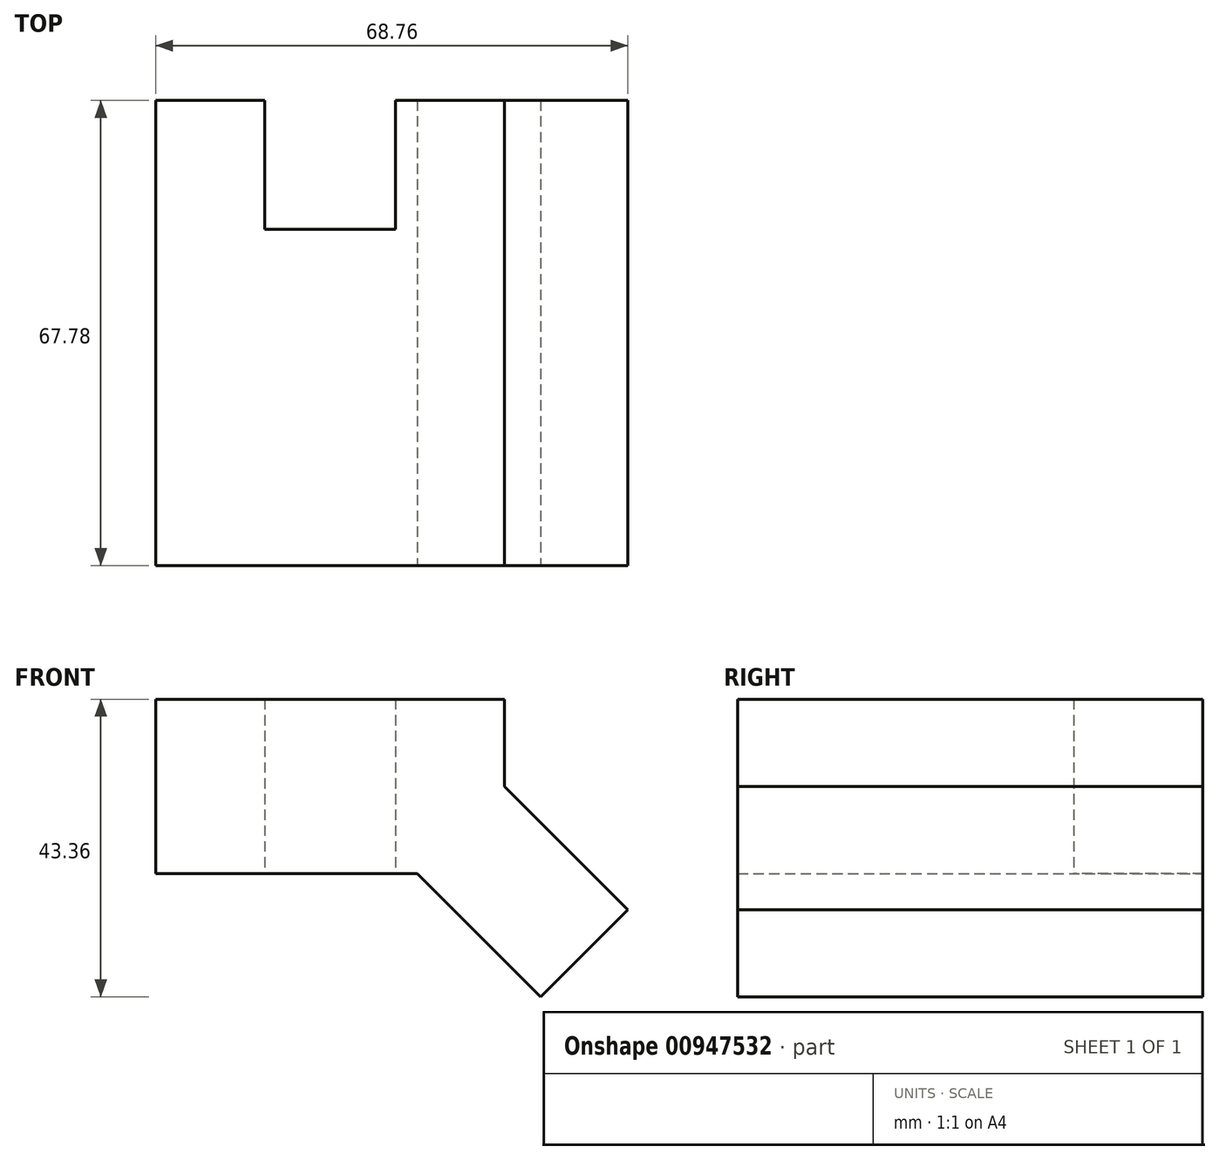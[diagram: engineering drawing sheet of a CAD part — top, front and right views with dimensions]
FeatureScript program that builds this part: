
annotation { "Feature Type Name" : "Feature", "Feature Type Description" : "" }
export const myFeature = defineFeature(function(context is Context, id is Id, definition is map)
    precondition{}
    {
        {
            var Q0;
            Q0=qCreatedBy(makeId("Top.planeOp"),FACE);
            var sketch = newSketch(context, id + "F0", { "sketchPlane" : qUnion([Q0])});
            skLineSegment(sketch, "E0.bottom", {"start": v(25.4, -33.9) * mm, "end": v(-25.4, -33.9) * mm});
            skLineSegment(sketch, "E0.top", {"start": v(25.4, 33.9) * mm, "end": v(-25.4, 33.9) * mm});
            skLineSegment(sketch, "E0.left", {"start": v(25.4, -33.9) * mm, "end": v(25.4, 33.9) * mm});
            skLineSegment(sketch, "E0.right", {"start": v(-25.4, -33.9) * mm, "end": v(-25.4, 33.9) * mm});
            skPoint(sketch, "E0.middle", {"position": v(0, 0) * mm});
            skLineSegment(sketch, "E1.bottom", {"start": v(-9.52, 33.9) * mm, "end": v(9.52, 33.9) * mm});
            skLineSegment(sketch, "E1.top", {"start": v(-9.52, 15.1) * mm, "end": v(9.53, 15.1) * mm});
            skLineSegment(sketch, "E1.left", {"start": v(-9.52, 33.9) * mm, "end": v(-9.52, 15.1) * mm});
            skLineSegment(sketch, "E1.right", {"start": v(9.53, 33.9) * mm, "end": v(9.53, 15.1) * mm});
            skPoint(sketch, "E2", {"position": v(-9.52, 33.9) * mm});
            skPoint(sketch, "E3", {"position": v(9.52, 33.9) * mm});
            skLineSegment(sketch, "E4", {"start": v(0, 45.23) * mm, "end": v(0, -39.07) * mm, "construction": true});
            skPoint(sketch, "E5", {"position": v(0, 15.1) * mm});
            skSolve(sketch);
        }
        {
            var Q0;
            Q0=makeQuery(id+"F0.imprint","IMPRINT",FACE,{"disambiguationData":[TD([[makeQuery(id+"F0.imprint","IMPRINT",EDGE,{"derivedFrom":sQuery(id+"F0.wireOp",EDGE,"E0.bottom")}),-1.0]])]});
            extrude(context, id + "F1", {"entities" : qUnion([Q0]), "depth" : 25.4 * mm, "offsetDistance" : 25.4 * mm});
        }
        {
            var Q0;
            Q0=makeQuery(id+"F1.opExtrude","CAP_EDGE",EDGE,{"disambiguationData":[OSD([sQuery(id+"F0.wireOp",EDGE,"E0.left")])],"isStart":true});
            chamfer(context, id + "F2", {"entities" : qUnion([Q0]), "width" : 12.7 * mm, "tangentPropagation" : true});
        }
        {
            var Q0;
            Q0=makeQuery(id+"F2.opChamfer","BLEND_FACE",FACE,{"disambiguationData":[OSD([sQuery(id+"F0.wireOp",EDGE,"E0.left")])]});
            extrude(context, id + "F3", {"entities" : qUnion([Q0]), "operationType" : NewBodyOperationType.ADD, "depth" : 25.4 * mm, "offsetDistance" : 25.4 * mm});
        }
    });
